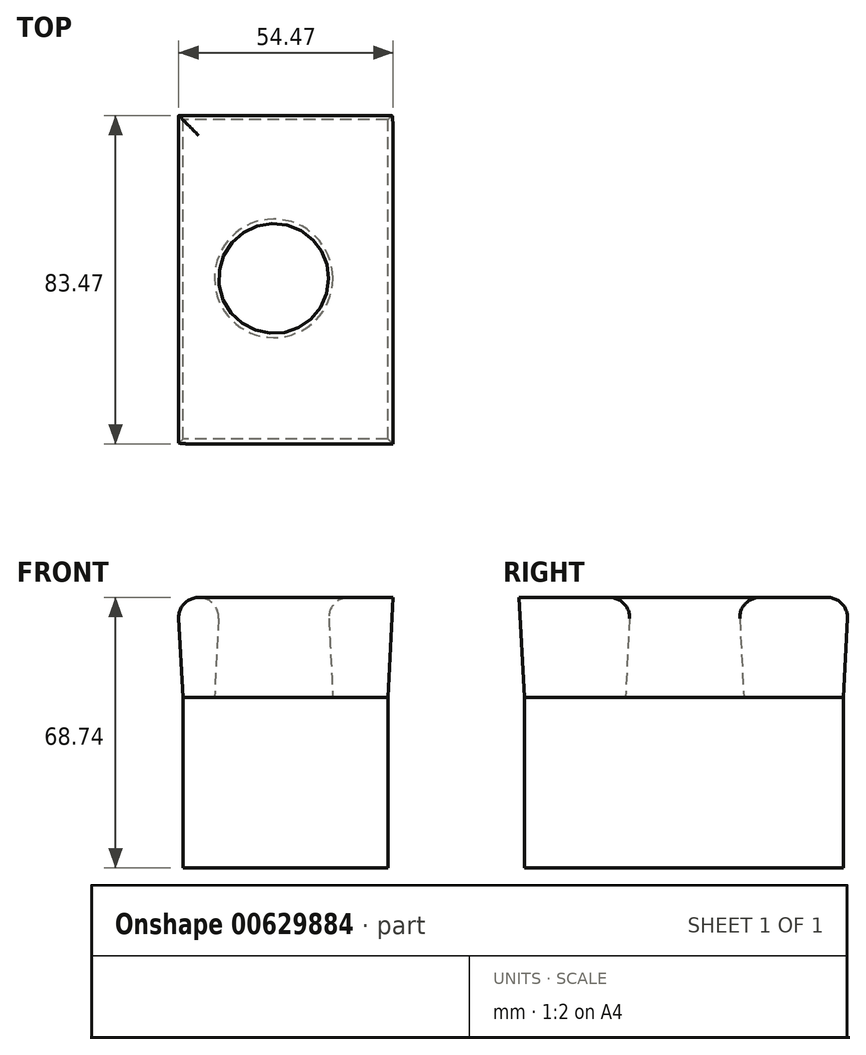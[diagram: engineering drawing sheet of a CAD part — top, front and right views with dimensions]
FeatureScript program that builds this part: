
annotation { "Feature Type Name" : "Feature", "Feature Type Description" : "" }
export const myFeature = defineFeature(function(context is Context, id is Id, definition is map)
    precondition{}
    {
        {
            var Q0;
            Q0=qCreatedBy(makeId("Top.planeOp"),FACE);
            var sketch = newSketch(context, id + "F0", { "sketchPlane" : qUnion([Q0])});
            skLineSegment(sketch, "E0.bottom", {"start": v(0, 0) * mm, "end": v(-52.08, 0) * mm});
            skLineSegment(sketch, "E0.top", {"start": v(0, 81.08) * mm, "end": v(-52.08, 81.08) * mm});
            skLineSegment(sketch, "E0.left", {"start": v(0, 0) * mm, "end": v(0, 81.08) * mm});
            skLineSegment(sketch, "E0.right", {"start": v(-52.08, 0) * mm, "end": v(-52.08, 81.08) * mm});
            skSolve(sketch);
        }
        {
            var Q0;
            Q0=makeQuery(id+"F0.imprint","IMPRINT",FACE,{"disambiguationData":[TD([[makeQuery(id+"F0.imprint","IMPRINT",EDGE,{"derivedFrom":sQuery(id+"F0.wireOp",EDGE,"E0.bottom")}),-1.0]])]});
            extrude(context, id + "F1", {"entities" : qUnion([Q0]), "depth" : 43.34 * mm, "offsetDistance" : 25.4 * mm});
        }
        {
            var Q0;
            Q0=makeQuery(id+"F1.opExtrude","CAP_FACE",FACE,{"disambiguationData":[OSD([sQuery(id+"F0.wireOp",EDGE,"E0.bottom"),sQuery(id+"F0.wireOp",EDGE,"E0.top"),sQuery(id+"F0.wireOp",EDGE,"E0.left"),sQuery(id+"F0.wireOp",EDGE,"E0.right")])],"isStart":false});
            var sketch = newSketch(context, id + "F2", { "sketchPlane" : qUnion([Q0])});
            skCircle(sketch, "E1", {"center": v(-28.99, 40.75) * mm, "radius": 15.04 * mm});
            skSolve(sketch);
        }
        {
            var Q0;
            Q0=makeQuery(id+"F2.imprint","IMPRINT",FACE,{"disambiguationData":[TD([[makeQuery(id+"F2.imprint","IMPRINT",EDGE,{"derivedFrom":sQuery(id+"F2.wireOp",EDGE,"E1")}),-1.0]])]});
            extrude(context, id + "F3", {"entities" : qUnion([Q0]), "operationType" : NewBodyOperationType.ADD, "depth" : 25.4 * mm, "offsetDistance" : 25.4 * mm, "hasDraft" : true, "draftAngle" : 3 * degree});
        }
        {
            var Q0;
            Q0=makeQuery(id+"F3.opExtrude","CAP_EDGE",EDGE,{"disambiguationData":[OSD([sQuery(id+"F0.wireOp",EDGE,"E0.top")])],"isStart":false});
            var Q1;
            Q1=makeQuery(id+"F3.opExtrude","CAP_EDGE",EDGE,{"disambiguationData":[OSD([sQuery(id+"F0.wireOp",EDGE,"E0.right")])],"isStart":false});
            fillet(context, id + "F4", {"entities" : qUnion([Q0, Q1]), "radius" : 5.08 * mm, "tangentPropagation" : true, "allowEdgeOverflow" : false});
        }
        {
            var Q0;
            Q0=makeQuery(id+"F3.opExtrude","CAP_EDGE",EDGE,{"disambiguationData":[OSD([sQuery(id+"F2.wireOp",EDGE,"E1")])],"isStart":false});
            fillet(context, id + "F5", {"entities" : qUnion([Q0]), "radius" : 5.08 * mm, "tangentPropagation" : true, "allowEdgeOverflow" : false});
        }
    });
